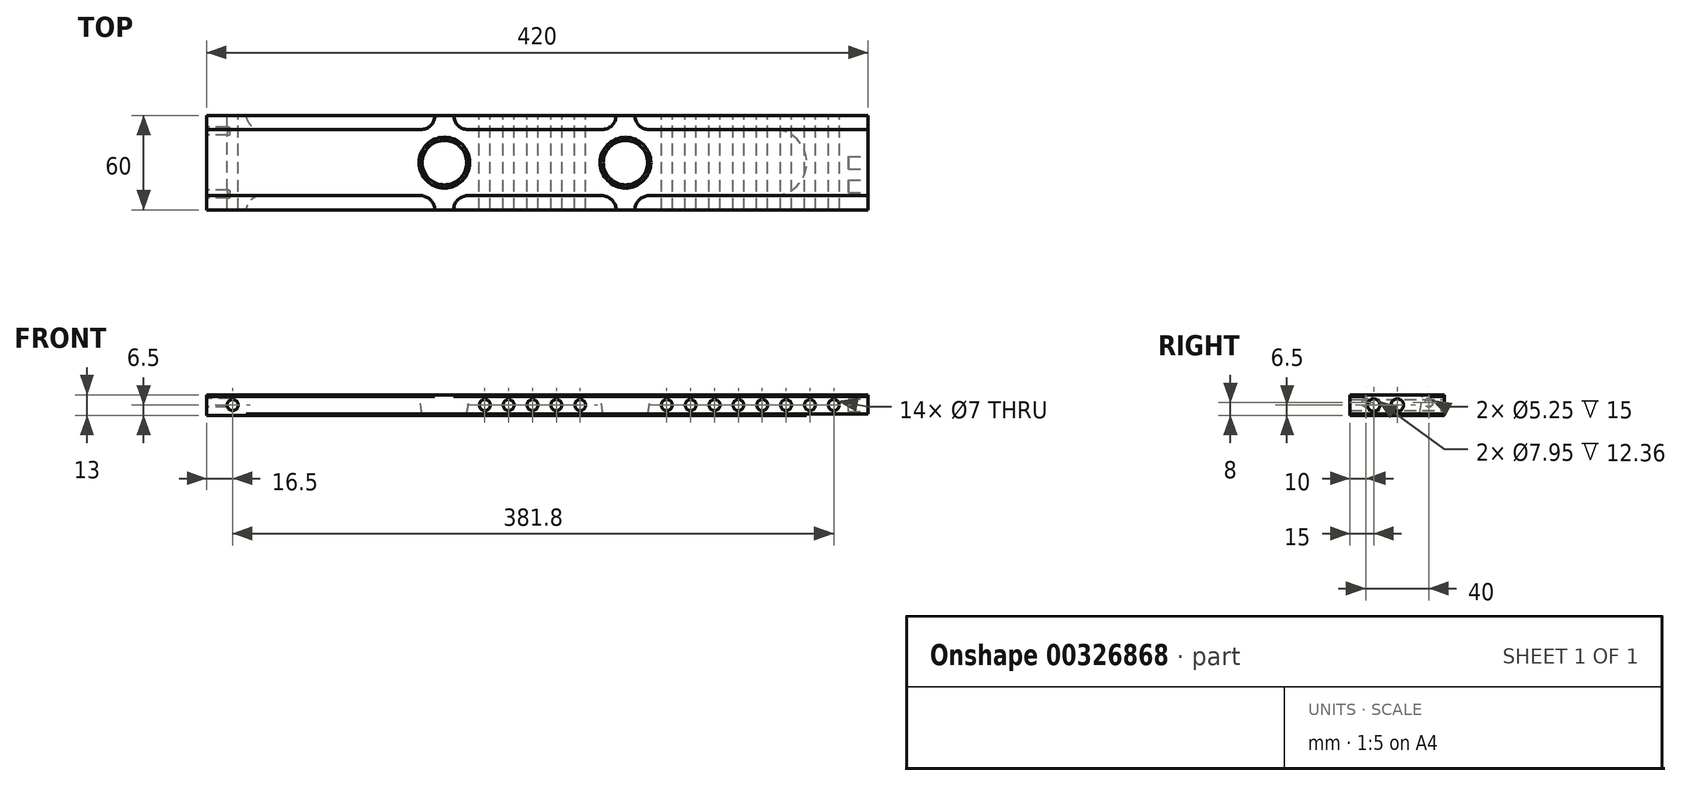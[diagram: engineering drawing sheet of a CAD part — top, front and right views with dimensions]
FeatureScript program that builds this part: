
annotation { "Feature Type Name" : "Feature", "Feature Type Description" : "" }
export const myFeature = defineFeature(function(context is Context, id is Id, definition is map)
    precondition{}
    {
        {
            var Q0;
            Q0=qCreatedBy(makeId("Top.planeOp"),FACE);
            var sketch = newSketch(context, id + "F0", { "sketchPlane" : qUnion([Q0])});
            skLineSegment(sketch, "E0.bottom", {"start": v(210, -30) * mm, "end": v(-210, -30) * mm});
            skLineSegment(sketch, "E0.top", {"start": v(210, 30) * mm, "end": v(-210, 30) * mm});
            skLineSegment(sketch, "E0.left", {"start": v(210, -30) * mm, "end": v(210, 30) * mm});
            skLineSegment(sketch, "E0.right", {"start": v(-210, -30) * mm, "end": v(-210, 30) * mm});
            skPoint(sketch, "E1.endSnap0", {"position": v(-210, 0) * mm});
            skPoint(sketch, "E2.endSnap0", {"position": v(210, 0) * mm});
            skLineSegment(sketch, "E3", {"start": v(-210, -30) * mm, "end": v(-210, -21) * mm});
            skLineSegment(sketch, "E4", {"start": v(-210, 30) * mm, "end": v(-210, 21) * mm});
            skSolve(sketch);
        }
        {
            var Q0;
            Q0=qSketchRegion(id+"F0",true);
            extrude(context, id + "F1", {"entities" : qUnion([Q0]), "depth" : 13 * mm});
        }
        {
            var Q0;
            Q0=makeQuery(id+"F1.opExtrude","CAP_FACE",FACE,{"disambiguationData":[OSD([sQuery(id+"F0.wireOp",EDGE,"E0.bottom"),sQuery(id+"F0.wireOp",EDGE,"E0.top"),sQuery(id+"F0.wireOp",EDGE,"E0.left"),sQuery(id+"F0.wireOp",EDGE,"E0.right"),sQuery(id+"F0.wireOp",EDGE,"E3"),sQuery(id+"F0.wireOp",EDGE,"E4")])],"isStart":false});
            var sketch = newSketch(context, id + "F2", { "sketchPlane" : qUnion([Q0])});
            skCircle(sketch, "E5", {"center": v(-59, 0) * mm, "radius": 16.1 * mm});
            skCircle(sketch, "E6", {"center": v(56, 0) * mm, "radius": 16.1 * mm});
            skPoint(sketch, "E6.centerSnap0", {"position": v(210, 0) * mm});
            skSolve(sketch);
        }
        {
            var Q0;
            Q0=makeQuery(id+"F2.imprint","IMPRINT",FACE,{"disambiguationData":[TD([[makeQuery(id+"F2.imprint","IMPRINT",EDGE,{"derivedFrom":sQuery(id+"F2.wireOp",EDGE,"E6")}),1.0]])]});
            var Q1;
            Q1=makeQuery(id+"F2.imprint","IMPRINT",FACE,{"disambiguationData":[TD([[makeQuery(id+"F2.imprint","IMPRINT",EDGE,{"derivedFrom":sQuery(id+"F2.wireOp",EDGE,"E5")}),1.0]])]});
            var Q2;
            Q2=sQuery(id+"F2.wireOp",EDGE,"E6");
            var Q3;
            Q3=sQuery(id+"F2.wireOp",EDGE,"E5");
            extrude(context, id + "F3", {"entities" : qUnion([Q0, Q1]), "operationType" : NewBodyOperationType.REMOVE, "surfaceEntities" : qUnion([Q2, Q3]), "oppositeDirection" : true, "depth" : 16 * mm, "hasDraft" : true, "draftAngle" : 8.7 * degree, "draftPullDirection" : true, "offsetDistance" : 25 * mm});
        }
        {
            var Q0;
            Q0=makeQuery(id+"F1.opExtrude","CAP_FACE",FACE,{"disambiguationData":[OSD([sQuery(id+"F0.wireOp",EDGE,"E0.bottom"),sQuery(id+"F0.wireOp",EDGE,"E0.top"),sQuery(id+"F0.wireOp",EDGE,"E0.left"),sQuery(id+"F0.wireOp",EDGE,"E0.right"),sQuery(id+"F0.wireOp",EDGE,"E3"),sQuery(id+"F0.wireOp",EDGE,"E4")])],"isStart":true});
            var sketch = newSketch(context, id + "F4", { "sketchPlane" : qUnion([Q0])});
            skPoint(sketch, "E7.middle", {"position": v(-210, 0) * mm});
            skLineSegment(sketch, "E8", {"start": v(-185, 30) * mm, "end": v(-185, 31) * mm});
            skLineSegment(sketch, "E9", {"start": v(-185, -30) * mm, "end": v(-185, -31) * mm});
            skLineSegment(sketch, "E10", {"start": v(-175, 21) * mm, "end": v(150, 21) * mm});
            skLineSegment(sketch, "E11", {"start": v(150, -21) * mm, "end": v(-175, -21) * mm});
            skArc(sketch, "E12", {"start": v(150, -21) * mm, "mid": v(171, 0) * mm, "end": v(150, 21) * mm});
            skPoint(sketch, "E13.visualSharp", {"position": v(-185, 21) * mm});
            skArc(sketch, "E13.filletArc", {"start": v(-185, 31) * mm, "mid": v(-182.07, 23.93) * mm, "end": v(-175, 21) * mm});
            skPoint(sketch, "E14.visualSharp", {"position": v(-185, -21) * mm});
            skArc(sketch, "E14.filletArc", {"start": v(-175, -21) * mm, "mid": v(-182.07, -23.93) * mm, "end": v(-185, -31) * mm});
            skSolve(sketch);
        }
        {
            var Q0;
            {var subQ1=sQuery(id+"F4.wireOp",EDGE,"E10");Q0=makeQuery(id+"F4.imprint","IMPRINT",FACE,{"disambiguationData":[TD([[makeQuery(id+"F4.imprint","IMPRINT",EDGE,{"derivedFrom":subQ1}),1.0]])]});}
            extrude(context, id + "F5", {"entities" : qUnion([Q0]), "operationType" : NewBodyOperationType.REMOVE, "oppositeDirection" : true, "depth" : 1 * mm});
        }
        {
            var Q0;
            Q0=makeQuery(id+"F1.opExtrude","SWEPT_FACE",FACE,{"disambiguationData":[OSD([sQuery(id+"F0.wireOp",EDGE,"E0.top")])]});
            var sketch = newSketch(context, id + "F6", { "sketchPlane" : qUnion([Q0])});
            skLineSegment(sketch, "E15", {"start": v(210, 6.5) * mm, "end": v(193.5, 6.5) * mm});
            skCircle(sketch, "E16", {"center": v(193.5, 6.5) * mm, "radius": 3.5 * mm});
            skLineSegment(sketch, "E17", {"start": v(193.5, 6.5) * mm, "end": v(33.35, 6.5) * mm});
            skCircle(sketch, "E18", {"center": v(33.35, 6.5) * mm, "radius": 3.5 * mm});
            skCircle(sketch, "E19.1.0.0", {"center": v(18.2, 6.5) * mm, "radius": 3.5 * mm});
            skCircle(sketch, "E19.2.0.0", {"center": v(3.05, 6.5) * mm, "radius": 3.5 * mm});
            skCircle(sketch, "E19.3.0.0", {"center": v(-12.1, 6.5) * mm, "radius": 3.5 * mm});
            skCircle(sketch, "E19.4.0.0", {"center": v(-27.25, 6.5) * mm, "radius": 3.5 * mm});
            skLineSegment(sketch, "E19.direction1", {"start": v(33.35, 6.5) * mm, "end": v(18.2, 6.5) * mm, "construction": true});
            skLineSegment(sketch, "E20", {"start": v(-27.25, 6.5) * mm, "end": v(-82.25, 6.5) * mm});
            skCircle(sketch, "E21", {"center": v(-82.25, 6.5) * mm, "radius": 3.5 * mm});
            skCircle(sketch, "E22.1.0.0", {"center": v(-97.4, 6.5) * mm, "radius": 3.5 * mm});
            skCircle(sketch, "E22.2.0.0", {"center": v(-112.55, 6.5) * mm, "radius": 3.5 * mm});
            skCircle(sketch, "E22.3.0.0", {"center": v(-127.7, 6.5) * mm, "radius": 3.5 * mm});
            skCircle(sketch, "E22.4.0.0", {"center": v(-142.85, 6.5) * mm, "radius": 3.5 * mm});
            skCircle(sketch, "E22.5.0.0", {"center": v(-158, 6.5) * mm, "radius": 3.5 * mm});
            skCircle(sketch, "E22.6.0.0", {"center": v(-173.15, 6.5) * mm, "radius": 3.5 * mm});
            skCircle(sketch, "E22.7.0.0", {"center": v(-188.3, 6.5) * mm, "radius": 3.5 * mm});
            skLineSegment(sketch, "E22.direction1", {"start": v(-82.25, 6.5) * mm, "end": v(-97.4, 6.5) * mm, "construction": true});
            skSolve(sketch);
        }
        {
            var Q0;
            Q0=qSketchRegion(id+"F6",true);
            extrude(context, id + "F7", {"entities" : qUnion([Q0]), "operationType" : NewBodyOperationType.REMOVE, "oppositeDirection" : true, "depth" : 60 * mm});
        }
        {
            var Q0;
            Q0=makeQuery(id+"F1.opExtrude","CAP_FACE",FACE,{"disambiguationData":[OSD([sQuery(id+"F0.wireOp",EDGE,"E0.bottom"),sQuery(id+"F0.wireOp",EDGE,"E0.top"),sQuery(id+"F0.wireOp",EDGE,"E0.left"),sQuery(id+"F0.wireOp",EDGE,"E0.right"),sQuery(id+"F0.wireOp",EDGE,"E3"),sQuery(id+"F0.wireOp",EDGE,"E4")])],"isStart":false});
            var sketch = newSketch(context, id + "F8", { "sketchPlane" : qUnion([Q0])});
            skPoint(sketch, "E23", {"position": v(-59, 0) * mm});
            skPoint(sketch, "E24", {"position": v(56, 0) * mm});
            skPoint(sketch, "E25.middle", {"position": v(-210, 0) * mm});
            skLineSegment(sketch, "E26", {"start": v(-65, 30) * mm, "end": v(-65, 30) * mm});
            skLineSegment(sketch, "E27", {"start": v(-53, 30) * mm, "end": v(-53, 30) * mm});
            skLineSegment(sketch, "E28", {"start": v(-65.17, -30) * mm, "end": v(-53.17, -30) * mm});
            skLineSegment(sketch, "E29", {"start": v(-65.17, -30) * mm, "end": v(-65.17, -30) * mm});
            skLineSegment(sketch, "E30", {"start": v(-53.17, -30) * mm, "end": v(-53.17, -30) * mm});
            skLineSegment(sketch, "E31", {"start": v(-44.17, -21) * mm, "end": v(41, -21) * mm});
            skLineSegment(sketch, "E32", {"start": v(50, -29.83) * mm, "end": v(50, -30) * mm});
            skLineSegment(sketch, "E33", {"start": v(62, -30) * mm, "end": v(62, -30) * mm});
            skLineSegment(sketch, "E34", {"start": v(-74.17, -21) * mm, "end": v(-210.17, -21) * mm});
            skPoint(sketch, "E35.visualSharp", {"position": v(-65, 21) * mm});
            skPoint(sketch, "E36.visualSharp", {"position": v(-53, 21) * mm});
            skArc(sketch, "E36.filletArc", {"start": v(-53, 30) * mm, "mid": v(-50.36, 23.63) * mm, "end": v(-44, 21) * mm});
            skPoint(sketch, "E37.visualSharp", {"position": v(49.83, -21) * mm});
            skArc(sketch, "E37.filletArc", {"start": v(50, -29.83) * mm, "mid": v(47.3, -23.58) * mm, "end": v(41, -21) * mm});
            skPoint(sketch, "E38.visualSharp", {"position": v(-53.17, -21) * mm});
            skArc(sketch, "E38.filletArc", {"start": v(-44.17, -21) * mm, "mid": v(-50.53, -23.64) * mm, "end": v(-53.17, -30) * mm});
            skPoint(sketch, "E39.visualSharp", {"position": v(-65.17, -21) * mm});
            skArc(sketch, "E39.filletArc", {"start": v(-65.17, -30) * mm, "mid": v(-67.8, -23.64) * mm, "end": v(-74.17, -21) * mm});
            skLineSegment(sketch, "E40", {"start": v(-74, 21) * mm, "end": v(-210, 21) * mm});
            skArc(sketch, "E41.filletArc", {"start": v(-74, 21) * mm, "mid": v(-67.64, 23.64) * mm, "end": v(-65, 30) * mm});
            skLineSegment(sketch, "E42", {"start": v(-65, 30) * mm, "end": v(-53, 30) * mm});
            skLineSegment(sketch, "E43", {"start": v(50, -30) * mm, "end": v(62, -30) * mm});
            skLineSegment(sketch, "E44.top", {"start": v(62, -30) * mm, "end": v(50, -30) * mm});
            skPoint(sketch, "E45.end.orphan", {"position": v(62, 21) * mm});
            skLineSegment(sketch, "E46", {"start": v(210, 21) * mm, "end": v(71, 21) * mm});
            skLineSegment(sketch, "E47", {"start": v(62, 30) * mm, "end": v(50, 30) * mm});
            skLineSegment(sketch, "E48", {"start": v(41, 21) * mm, "end": v(-44, 21) * mm});
            skLineSegment(sketch, "E49", {"start": v(50, 30) * mm, "end": v(50, 30) * mm});
            skPoint(sketch, "E50.visualSharp", {"position": v(50, 21) * mm});
            skArc(sketch, "E50.filletArc", {"start": v(41, 21) * mm, "mid": v(47.36, 23.64) * mm, "end": v(50, 30) * mm});
            skLineSegment(sketch, "E51", {"start": v(62, 30) * mm, "end": v(62, 30) * mm});
            skArc(sketch, "E52.filletArc", {"start": v(62, 30) * mm, "mid": v(64.64, 23.64) * mm, "end": v(71, 21) * mm});
            skLineSegment(sketch, "E53", {"start": v(71, -21) * mm, "end": v(210, -21) * mm});
            skPoint(sketch, "E53.endSnap0", {"position": v(210, 0) * mm});
            skPoint(sketch, "E54.visualSharp", {"position": v(62, -21) * mm});
            skArc(sketch, "E54.filletArc", {"start": v(71, -21) * mm, "mid": v(64.64, -23.64) * mm, "end": v(62, -30) * mm});
            skSolve(sketch);
        }
        {
            var Q0;
            {var subQ0=sQuery(id+"F8.wireOp",EDGE,"E46");Q0=makeQuery(id+"F8.imprint","IMPRINT",FACE,{"disambiguationData":[TD([[makeQuery(id+"F8.imprint","IMPRINT",EDGE,{"derivedFrom":subQ0}),-1.0]])]});}
            extrude(context, id + "F9", {"entities" : qUnion([Q0]), "operationType" : NewBodyOperationType.REMOVE, "oppositeDirection" : true, "depth" : 1 * mm});
        }
        {
            var Q0;
            {var subQ0=sQuery(id+"F8.wireOp",EDGE,"E53");Q0=makeQuery(id+"F8.imprint","IMPRINT",FACE,{"disambiguationData":[TD([[makeQuery(id+"F8.imprint","IMPRINT",EDGE,{"derivedFrom":subQ0}),-1.0]])]});}
            var Q1;
            Q1=makeQuery(id+"F8.imprint","IMPRINT",FACE,{"disambiguationData":[TD([[makeQuery(id+"F8.imprint","IMPRINT",EDGE,{"derivedFrom":sQuery(id+"F8.wireOp",EDGE,"E31")}),-1.0]])]});
            extrude(context, id + "F10", {"entities" : qUnion([Q0, Q1]), "operationType" : NewBodyOperationType.REMOVE, "oppositeDirection" : true, "depth" : 1 * mm});
        }
        {
            var Q0;
            {var subQ0=sQuery(id+"F8.wireOp",EDGE,"E39.filletArc");Q0=makeQuery(id+"F8.imprint","IMPRINT",FACE,{"disambiguationData":[TD([[makeQuery(id+"F8.imprint","IMPRINT",EDGE,{"derivedFrom":subQ0}),1.0]])]});}
            var Q1;
            {var subQ6=sQuery(id+"F8.wireOp",EDGE,"E40");Q1=makeQuery(id+"F8.imprint","IMPRINT",FACE,{"disambiguationData":[TD([[makeQuery(id+"F8.imprint","IMPRINT",EDGE,{"derivedFrom":subQ6}),-1.0]])]});}
            extrude(context, id + "F11", {"entities" : qUnion([Q0, Q1]), "operationType" : NewBodyOperationType.REMOVE, "oppositeDirection" : true, "depth" : 1 * mm});
        }
        {
            var Q0;
            {var subQ1=sQuery(id+"F8.wireOp",EDGE,"E27");Q0=makeQuery(id+"F8.imprint","IMPRINT",FACE,{"disambiguationData":[TD([[makeQuery(id+"F8.imprint","IMPRINT",EDGE,{"derivedFrom":subQ1}),1.0]])]});}
            extrude(context, id + "F12", {"entities" : qUnion([Q0]), "operationType" : NewBodyOperationType.REMOVE, "oppositeDirection" : true, "depth" : 1 * mm});
        }
        {
            var Q0;
            Q0=makeQuery(id+"F1.opExtrude","SWEPT_FACE",FACE,{"disambiguationData":[OSD([sQuery(id+"F0.wireOp",EDGE,"E0.right"),sQuery(id+"F0.wireOp",EDGE,"E3"),sQuery(id+"F0.wireOp",EDGE,"E4")])]});
            var sketch = newSketch(context, id + "F13", { "sketchPlane" : qUnion([Q0])});
            skCircle(sketch, "E55", {"center": v(-20, 8) * mm, "radius": 2.62 * mm});
            skCircle(sketch, "E56", {"center": v(20, 8) * mm, "radius": 2.62 * mm});
            skSolve(sketch);
        }
        {
            var Q0;
            Q0=makeQuery(id+"F13.imprint","IMPRINT",FACE,{"disambiguationData":[TD([[makeQuery(id+"F13.imprint","IMPRINT",EDGE,{"derivedFrom":sQuery(id+"F13.wireOp",EDGE,"E55")}),1.0]])]});
            var Q1;
            Q1=makeQuery(id+"F13.imprint","IMPRINT",FACE,{"disambiguationData":[TD([[makeQuery(id+"F13.imprint","IMPRINT",EDGE,{"derivedFrom":sQuery(id+"F13.wireOp",EDGE,"E56")}),1.0]])]});
            var Q2;
            Q2=sQuery(id+"F13.wireOp",EDGE,"E55");
            var Q3;
            Q3=sQuery(id+"F13.wireOp",EDGE,"E56");
            extrude(context, id + "F14", {"entities" : qUnion([Q0, Q1]), "operationType" : NewBodyOperationType.REMOVE, "surfaceEntities" : qUnion([Q2, Q3]), "oppositeDirection" : true, "depth" : 15 * mm});
        }
        {
            var Q0;
            Q0=makeQuery(id+"F1.opExtrude","SWEPT_FACE",FACE,{"disambiguationData":[OSD([sQuery(id+"F0.wireOp",EDGE,"E0.left")])]});
            var sketch = newSketch(context, id + "F15", { "sketchPlane" : qUnion([Q0])});
            skCircle(sketch, "E57", {"center": v(-15, 6.5) * mm, "radius": 3.98 * mm});
            skPoint(sketch, "E57.centerSnap0", {"position": v(-30, 6.5) * mm});
            skCircle(sketch, "E58", {"center": v(0, 6.5) * mm, "radius": 3.98 * mm});
            skPoint(sketch, "E58.centerSnap0", {"position": v(30, 6.5) * mm});
            skSolve(sketch);
        }
        {
            var Q0;
            Q0=makeQuery(id+"F15.imprint","IMPRINT",FACE,{"disambiguationData":[TD([[makeQuery(id+"F15.imprint","IMPRINT",EDGE,{"derivedFrom":sQuery(id+"F15.wireOp",EDGE,"E58")}),1.0]])]});
            var Q1;
            Q1=makeQuery(id+"F15.imprint","IMPRINT",FACE,{"disambiguationData":[TD([[makeQuery(id+"F15.imprint","IMPRINT",EDGE,{"derivedFrom":sQuery(id+"F15.wireOp",EDGE,"E57")}),1.0]])]});
            extrude(context, id + "F16", {"entities" : qUnion([Q0, Q1]), "operationType" : NewBodyOperationType.REMOVE, "oppositeDirection" : true, "depth" : 12.36 * mm});
        }
    });
